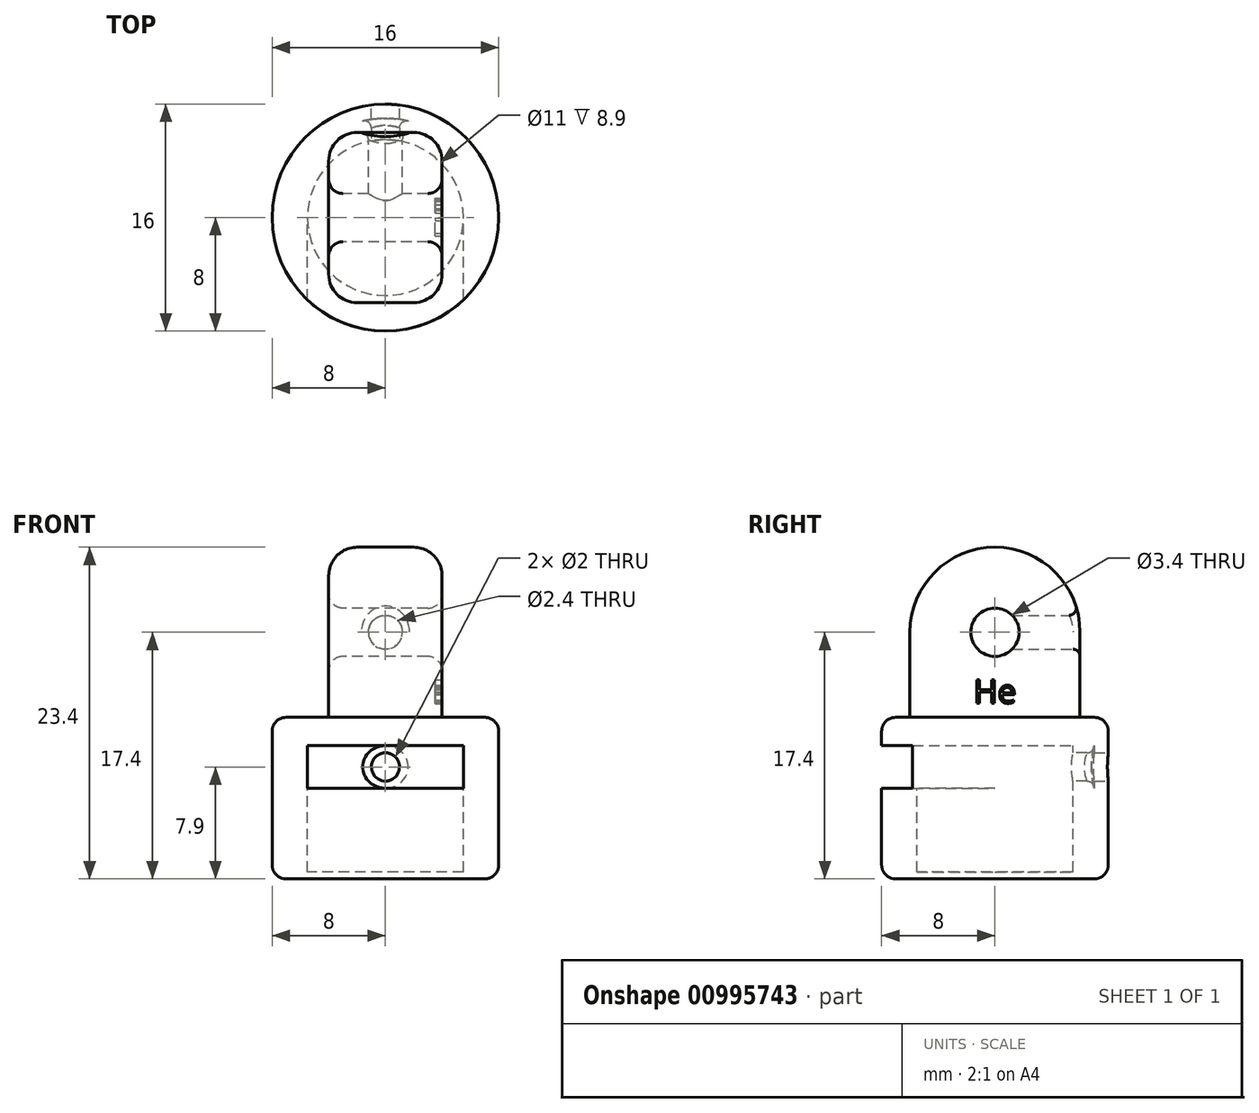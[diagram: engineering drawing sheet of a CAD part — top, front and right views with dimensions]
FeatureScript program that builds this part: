
annotation { "Feature Type Name" : "Feature", "Feature Type Description" : "" }
export const myFeature = defineFeature(function(context is Context, id is Id, definition is map)
    precondition{}
    {
        {
            var Q0;
            Q0=qCreatedBy(makeId("Top.planeOp"),FACE);
            var sketch = newSketch(context, id + "F0", { "sketchPlane" : qUnion([Q0])});
            skCircle(sketch, "E0", {"center": v(0, 0) * mm, "radius": 7 * mm});
            skSolve(sketch);
        }
        {
            var Q0;
            Q0 = qSketchRegion(id + "F0", true);
            extrude(context, id + "F1", {"entities" : qUnion([Q0]), "depth" : 9.4 * mm, "offsetDistance" : 25 * mm});
        }
        {
            var Q0;
            Q0=makeQuery(id+"F1.opExtrude","CAP_FACE",FACE,{"disambiguationData":[OSD([sQuery(id+"F0.wireOp",EDGE,"E0")])],"isStart":false});
            var sketch = newSketch(context, id + "F2", { "sketchPlane" : qUnion([Q0])});
            skCircle(sketch, "E1", {"center": v(0, 0) * mm, "radius": 5.5 * mm});
            skSolve(sketch);
        }
        {
            var Q0;
            Q0 = qSketchRegion(id + "F2", true);
            extrude(context, id + "F3", {"entities" : qUnion([Q0]), "operationType" : NewBodyOperationType.REMOVE, "oppositeDirection" : true, "depth" : 8.9 * mm, "offsetDistance" : 25 * mm});
        }
        {
            var Q0;
            Q0=makeQuery(id+"F1.opExtrude","CAP_FACE",FACE,{"disambiguationData":[OSD([sQuery(id+"F0.wireOp",EDGE,"E0")])],"isStart":false});
            var sketch = newSketch(context, id + "F4", { "sketchPlane" : qUnion([Q0])});
            skLineSegment(sketch, "E2.bottom", {"start": v(5.5, -10) * mm, "end": v(-5.5, -10) * mm});
            skLineSegment(sketch, "E2.top", {"start": v(5.5, 0) * mm, "end": v(-5.5, 0) * mm});
            skLineSegment(sketch, "E2.left", {"start": v(5.5, -10) * mm, "end": v(5.5, 0) * mm});
            skLineSegment(sketch, "E2.right", {"start": v(-5.5, -10) * mm, "end": v(-5.5, 0) * mm});
            skPoint(sketch, "E2.middle", {"position": v(0, -5) * mm});
            skSolve(sketch);
        }
        {
            var Q0;
            Q0 = qSketchRegion(id + "F4", true);
            extrude(context, id + "F5", {"entities" : qUnion([Q0]), "operationType" : NewBodyOperationType.REMOVE, "oppositeDirection" : true, "depth" : 3 * mm, "offsetDistance" : 25 * mm});
        }
        {
            var Q0;
            Q0=makeQuery(id+"F1.opExtrude","CAP_FACE",FACE,{"disambiguationData":[OSD([sQuery(id+"F0.wireOp",EDGE,"E0")])],"isStart":false});
            var sketch = newSketch(context, id + "F6", { "sketchPlane" : qUnion([Q0])});
            skCircle(sketch, "E3", {"center": v(0, 0) * mm, "radius": 7 * mm});
            skSolve(sketch);
        }
        {
            var Q0;
            Q0 = qSketchRegion(id + "F6", true);
            extrude(context, id + "F7", {"entities" : qUnion([Q0]), "operationType" : NewBodyOperationType.ADD, "depth" : 2 * mm, "offsetDistance" : 25 * mm});
        }
        {
            var Q0;
            Q0=qCreatedBy(makeId("Front.planeOp"),FACE);
            var sketch = newSketch(context, id + "F8", { "sketchPlane" : qUnion([Q0])});
            skCircle(sketch, "E4", {"center": v(0, 7.9) * mm, "radius": 1 * mm});
            skSolve(sketch);
        }
        {
            var Q0;
            Q0 = qSketchRegion(id + "F8", true);
            extrude(context, id + "F9", {"entities" : qUnion([Q0]), "operationType" : NewBodyOperationType.REMOVE, "endBound" : BoundingType.SYMMETRIC, "oppositeDirection" : true, "depth" : 25 * mm, "offsetDistance" : 25 * mm});
        }
        {
            var Q0;
            Q0=qCreatedBy(makeId("Right.planeOp"),FACE);
            var sketch = newSketch(context, id + "F10", { "sketchPlane" : qUnion([Q0])});
            skLineSegment(sketch, "E5.top", {"start": v(6, 11.4) * mm, "end": v(-6, 11.4) * mm});
            skLineSegment(sketch, "E5.left", {"start": v(6, 17.4) * mm, "end": v(6, 11.4) * mm});
            skLineSegment(sketch, "E5.right", {"start": v(-6, 17.4) * mm, "end": v(-6, 11.4) * mm});
            skPoint(sketch, "E5.middle", {"position": v(0, 14.4) * mm});
            skArc(sketch, "E6", {"start": v(6, 17.4) * mm, "mid": v(0, 23.4) * mm, "end": v(-6, 17.4) * mm});
            skCircle(sketch, "E7", {"center": v(0, 17.4) * mm, "radius": 1.7 * mm});
            skSolve(sketch);
        }
        {
            var Q0;
            Q0=makeQuery(id+"F10.imprint","IMPRINT",FACE,{"disambiguationData":[TD([[makeQuery(id+"F10.imprint","IMPRINT",EDGE,{"derivedFrom":sQuery(id+"F10.wireOp",EDGE,"E5.top")}),-1.0]])]});
            extrude(context, id + "F11", {"entities" : qUnion([Q0]), "operationType" : NewBodyOperationType.ADD, "endBound" : BoundingType.SYMMETRIC, "depth" : 8 * mm, "offsetDistance" : 25 * mm});
        }
        {
            var Q0;
            Q0=makeQuery(id+"F11.opExtrude","SWEPT_FACE",FACE,{"disambiguationData":[OSD([sQuery(id+"F10.wireOp",EDGE,"E5.left")])]});
            var sketch = newSketch(context, id + "F12", { "sketchPlane" : qUnion([Q0])});
            skCircle(sketch, "E8", {"center": v(0, 17.4) * mm, "radius": 1.2 * mm});
            skSolve(sketch);
        }
        {
            var Q0;
            Q0 = qSketchRegion(id + "F12", true);
            extrude(context, id + "F13", {"entities" : qUnion([Q0]), "operationType" : NewBodyOperationType.REMOVE, "endBound" : BoundingType.UP_TO_NEXT, "oppositeDirection" : true, "depth" : 25 * mm, "offsetDistance" : 25 * mm});
        }
        {
            var Q0;
            Q0=makeQuery(id+"F11.opExtrude","CAP_EDGE",EDGE,{"disambiguationData":[OSD([sQuery(id+"F10.wireOp",EDGE,"E6")])],"isStart":false});
            var Q1;
            Q1=makeQuery(id+"F11.opExtrude","CAP_EDGE",EDGE,{"disambiguationData":[OSD([sQuery(id+"F10.wireOp",EDGE,"E5.left")])],"isStart":false});
            var Q2;
            Q2=makeQuery(id+"F11.opExtrude","CAP_EDGE",EDGE,{"disambiguationData":[OSD([sQuery(id+"F10.wireOp",EDGE,"E5.right")])],"isStart":false});
            fillet(context, id + "F14", {"entities" : qUnion([Q0, Q1, Q2]), "radius" : 2 * mm, "tangentPropagation" : true, "allowEdgeOverflow" : false});
        }
        {
            var Q0;
            Q0=makeQuery(id+"F11.opExtrude","CAP_EDGE",EDGE,{"disambiguationData":[OSD([sQuery(id+"F10.wireOp",EDGE,"E5.left")])],"isStart":true});
            var Q1;
            Q1=makeQuery(id+"F11.opExtrude","CAP_EDGE",EDGE,{"disambiguationData":[OSD([sQuery(id+"F10.wireOp",EDGE,"E5.right")])],"isStart":true});
            var Q2;
            Q2=makeQuery(id+"F11.opExtrude","CAP_EDGE",EDGE,{"disambiguationData":[OSD([sQuery(id+"F10.wireOp",EDGE,"E6")])],"isStart":true});
            fillet(context, id + "F15", {"entities" : qUnion([Q0, Q1, Q2]), "radius" : 2 * mm, "tangentPropagation" : true, "allowEdgeOverflow" : false});
        }
        {
            var Q0;
            Q0=makeQuery(id+"F11.opExtrude","CAP_EDGE",EDGE,{"disambiguationData":[OSD([sQuery(id+"F10.wireOp",EDGE,"E7")])],"isStart":true});
            var Q1;
            Q1=makeQuery(id+"F11.opExtrude","CAP_EDGE",EDGE,{"disambiguationData":[OSD([sQuery(id+"F10.wireOp",EDGE,"E7")])],"isStart":false});
            fillet(context, id + "F16", {"entities" : qUnion([Q0, Q1]), "radius" : 1 * mm, "tangentPropagation" : true, "allowEdgeOverflow" : false});
        }
        {
            var Q0;
            Q0=makeQuery(id+"F9.boolean.opBoolean","INTERSECT",EDGE,{"derivedFrom":[makeQuery(id+"F7.boolean.opBoolean","MERGE",FACE,{"derivedFrom":[makeQuery(id+"F1.opExtrude","SWEPT_FACE",FACE,{"disambiguationData":[OSD([sQuery(id+"F0.wireOp",EDGE,"E0")])]}),makeQuery(id+"F7.opExtrude","SWEPT_FACE",FACE,{"disambiguationData":[OSD([sQuery(id+"F6.wireOp",EDGE,"E3")])]})]}),makeQuery(id+"F9.opExtrude","SWEPT_FACE",FACE,{"disambiguationData":[OSD([sQuery(id+"F8.wireOp",EDGE,"E4")])]})]});
            fillet(context, id + "F17", {"entities" : qUnion([Q0]), "radius" : .5 * mm, "tangentPropagation" : true, "allowEdgeOverflow" : false});
        }
        {
            var Q0;
            Q0=makeQuery(id+"F13.boolean.opBoolean","INTERSECT",EDGE,{"derivedFrom":[makeQuery(id+"F11.opExtrude","SWEPT_FACE",FACE,{"disambiguationData":[OSD([sQuery(id+"F10.wireOp",EDGE,"E6")])]}),makeQuery(id+"F13.opExtrude","SWEPT_FACE",FACE,{"disambiguationData":[OSD([sQuery(id+"F12.wireOp",EDGE,"E8")])]})]});
            var Q1;
            Q1=makeQuery(id+"F13.boolean.opBoolean","COPY",EDGE,{"derivedFrom":makeQuery(id+"F13.opExtrude","CAP_EDGE",EDGE,{"disambiguationData":[OSD([sQuery(id+"F12.wireOp",EDGE,"E8")])],"isStart":true})});
            fillet(context, id + "F18", {"entities" : qUnion([Q0, Q1]), "radius" : .5 * mm, "tangentPropagation" : true, "allowEdgeOverflow" : false});
        }
        {
            var Q0;
            Q0=makeQuery(id+"F11.opExtrude","CAP_FACE",FACE,{"disambiguationData":[OSD([sQuery(id+"F10.wireOp",EDGE,"E5.top"),sQuery(id+"F10.wireOp",EDGE,"E5.left"),sQuery(id+"F10.wireOp",EDGE,"E5.right"),sQuery(id+"F10.wireOp",EDGE,"E6"),sQuery(id+"F10.wireOp",EDGE,"E7")])],"isStart":false});
            var sketch = newSketch(context, id + "F19", { "sketchPlane" : qUnion([Q0])});
            skText(sketch, "E9", { "text": "He", "fontName": "OpenSans-Regular.ttf"});
            const initialGuessF19  = {"E9": [-0.00152, 0.0124, 1, 0, 0.00167]};
            skSetInitialGuess(sketch, initialGuessF19);
            skSolve(sketch);
        }
        {
            var Q0;
            Q0 = qSketchRegion(id + "F19", true);
            extrude(context, id + "F20", {"entities" : qUnion([Q0]), "operationType" : NewBodyOperationType.REMOVE, "oppositeDirection" : true, "depth" : .5 * mm, "offsetDistance" : 25 * mm});
        }
        {
            var Q0;
            Q0=qCreatedBy(makeId("Top.planeOp"),FACE);
            var sketch = newSketch(context, id + "F21", { "sketchPlane" : qUnion([Q0])});
            skCircle(sketch, "E10", {"center": v(0, 0) * mm, "radius": 8 * mm});
            skCircle(sketch, "E11", {"center": v(0, 0) * mm, "radius": 7 * mm});
            skSolve(sketch);
        }
        {
            var Q0;
            Q0 = qSketchRegion(id + "F21", true);
            extrude(context, id + "F22", {"entities" : qUnion([Q0]), "operationType" : NewBodyOperationType.ADD, "depth" : 11.4 * mm, "offsetDistance" : 25 * mm});
        }
        {
            var Q0;
            Q0 = qSketchRegion(id + "F4", true);
            extrude(context, id + "F23", {"entities" : qUnion([Q0]), "operationType" : NewBodyOperationType.REMOVE, "oppositeDirection" : true, "depth" : 3 * mm, "offsetDistance" : 25 * mm});
        }
        {
            var Q0;
            Q0 = qSketchRegion(id + "F8", true);
            extrude(context, id + "F24", {"entities" : qUnion([Q0]), "operationType" : NewBodyOperationType.REMOVE, "endBound" : BoundingType.SYMMETRIC, "depth" : 25 * mm, "offsetDistance" : 25 * mm});
        }
        {
            var Q0;
            Q0=makeQuery(id+"F22.opExtrude","CAP_EDGE",EDGE,{"disambiguationData":[OSD([sQuery(id+"F21.wireOp",EDGE,"E10")])],"isStart":false});
            fillet(context, id + "F25", {"entities" : qUnion([Q0]), "radius" : 1 * mm, "tangentPropagation" : true, "allowEdgeOverflow" : false});
        }
        {
            var Q0;
            Q0=makeQuery(id+"F22.opExtrude","CAP_EDGE",EDGE,{"disambiguationData":[OSD([sQuery(id+"F21.wireOp",EDGE,"E10")])],"isStart":true});
            fillet(context, id + "F26", {"entities" : qUnion([Q0]), "radius" : 1 * mm, "tangentPropagation" : true, "allowEdgeOverflow" : false});
        }
    });
